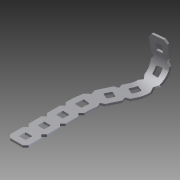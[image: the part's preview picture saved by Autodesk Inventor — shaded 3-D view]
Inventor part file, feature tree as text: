
AUTODESK INVENTOR PART (.ipt)
format: ipt  version: 2014 SP1 (Build 180222100, 222)  size: 579,072 bytes
history: native  units: in
note: dims shown in document units (in); Inventor stores cm internally (conversion verified against a paired STEP export)
features: sketch x4, other x3
ambient origin geometry x8: Origin, YZ Plane, XZ Plane, XY Plane, X Axis, Y Axis, Z Axis, Center Point
bodies: Solid1 (feature_tree)
feature tree (7):
  other  "metal that keeps pto together.ipt"
  other  "NONE::metal that keeps pto together.ipt"
  other  "TaggingFeature1"
  sketch  "Sketch1"  dims[d0=0.3937in]
  sketch  "Sketch2"  dims[d1=1.0in d2=0.0in d3=0.5in d4=0.6528in d5=0.1787in d6=0.5in d7=0.1787in d8=0.5in]
  sketch  "Sketch4"
  sketch  "Sketch5"
